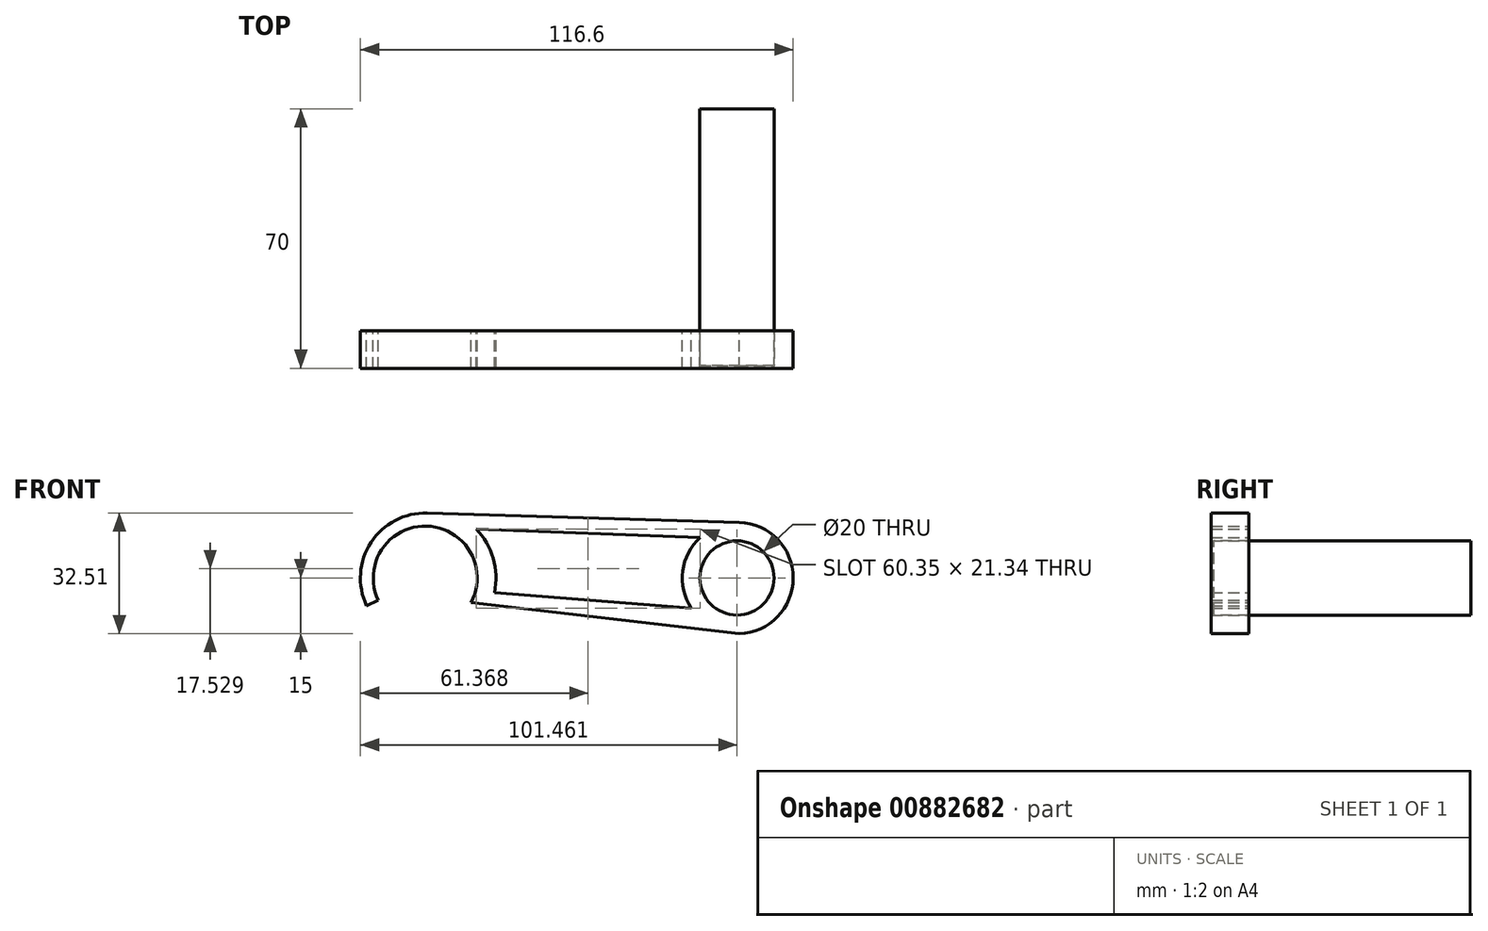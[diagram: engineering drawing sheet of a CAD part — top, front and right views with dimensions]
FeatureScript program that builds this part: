
annotation { "Feature Type Name" : "Feature", "Feature Type Description" : "" }
export const myFeature = defineFeature(function(context is Context, id is Id, definition is map)
    precondition{}
    {
        {
            var Q0;
            Q0=qCreatedBy(makeId("Front.planeOp"),FACE);
            var sketch = newSketch(context, id + "F0", { "sketchPlane" : qUnion([Q0])});
            skLineSegment(sketch, "E0.bottom", {"start": v(-29.75, 17.5) * mm, "end": v(54.26, 15) * mm});
            skCircle(sketch, "E1", {"center": v(53.68, 0) * mm, "radius": 10 * mm});
            skArc(sketch, "E2", {"start": v(-17.97, -6.6) * mm, "mid": v(-29.96, 14) * mm, "end": v(-42.99, -5.96) * mm});
            skArc(sketch, "E3", {"start": v(54.26, 15) * mm, "mid": v(68.82, 0) * mm, "end": v(54.26, -15) * mm});
            skArc(sketch, "E4", {"start": v(-29.75, 17.5) * mm, "mid": v(-44.92, 9.6) * mm, "end": v(-46.1, -7.47) * mm});
            skLineSegment(sketch, "E5", {"start": v(-46.1, -7.47) * mm, "end": v(-42.99, -5.96) * mm});
            skLineSegment(sketch, "E6", {"start": v(-17.97, -6.6) * mm, "end": v(54.26, -15) * mm});
            skArc(sketch, "E7", {"start": v(-16.58, 13.2) * mm, "mid": v(-12, 5.25) * mm, "end": v(-11.67, -3.93) * mm});
            skArc(sketch, "E8", {"start": v(43.76, 10.96) * mm, "mid": v(39.06, 1.85) * mm, "end": v(41.37, -8.14) * mm});
            skLineSegment(sketch, "E9", {"start": v(-16.58, 13.2) * mm, "end": v(43.76, 10.96) * mm});
            skLineSegment(sketch, "E10", {"start": v(-11.67, -3.93) * mm, "end": v(41.37, -8.14) * mm});
            skSolve(sketch);
        }
        {
            var Q0;
            Q0 = qSketchRegion(id + "F0", true);
            extrude(context, id + "F1", {"entities" : qUnion([Q0]), "depth" : 10.2 * mm, "offsetDistance" : 25 * mm});
        }
        {
            var Q0;
            Q0=makeQuery(id+"F1.opExtrude","CAP_FACE",FACE,{"disambiguationData":[OSD([sQuery(id+"F0.wireOp",EDGE,"E0.bottom"),sQuery(id+"F0.wireOp",EDGE,"E1"),sQuery(id+"F0.wireOp",EDGE,"E2"),sQuery(id+"F0.wireOp",EDGE,"E3"),sQuery(id+"F0.wireOp",EDGE,"E4"),sQuery(id+"F0.wireOp",EDGE,"E5"),sQuery(id+"F0.wireOp",EDGE,"E6"),sQuery(id+"F0.wireOp",EDGE,"E7"),sQuery(id+"F0.wireOp",EDGE,"E8"),sQuery(id+"F0.wireOp",EDGE,"E9"),sQuery(id+"F0.wireOp",EDGE,"E10")])],"isStart":false});
            var sketch = newSketch(context, id + "F2", { "sketchPlane" : qUnion([Q0])});
            skSolve(sketch);
        }
        {
            var Q0;
            Q0=makeQuery(id+"F2.imprint","IMPRINT",FACE,{"disambiguationData":[TD([[makeQuery(id+"F2.imprint","IMPRINT",EDGE,{"derivedFrom":makeQuery(id+"F1.opExtrude","CAP_EDGE",EDGE,{"disambiguationData":[OSD([sQuery(id+"F0.wireOp",EDGE,"E1")])],"isStart":false})}),1.0]])]});
            extrude(context, id + "F3", {"entities" : qUnion([Q0]), "oppositeDirection" : true, "depth" : 70 * mm, "offsetDistance" : 25 * mm, "hasSecondDirection" : true, "secondDirectionOppositeDirection" : true, "secondDirectionDepth" : 0.8 * mm});
        }
    });
